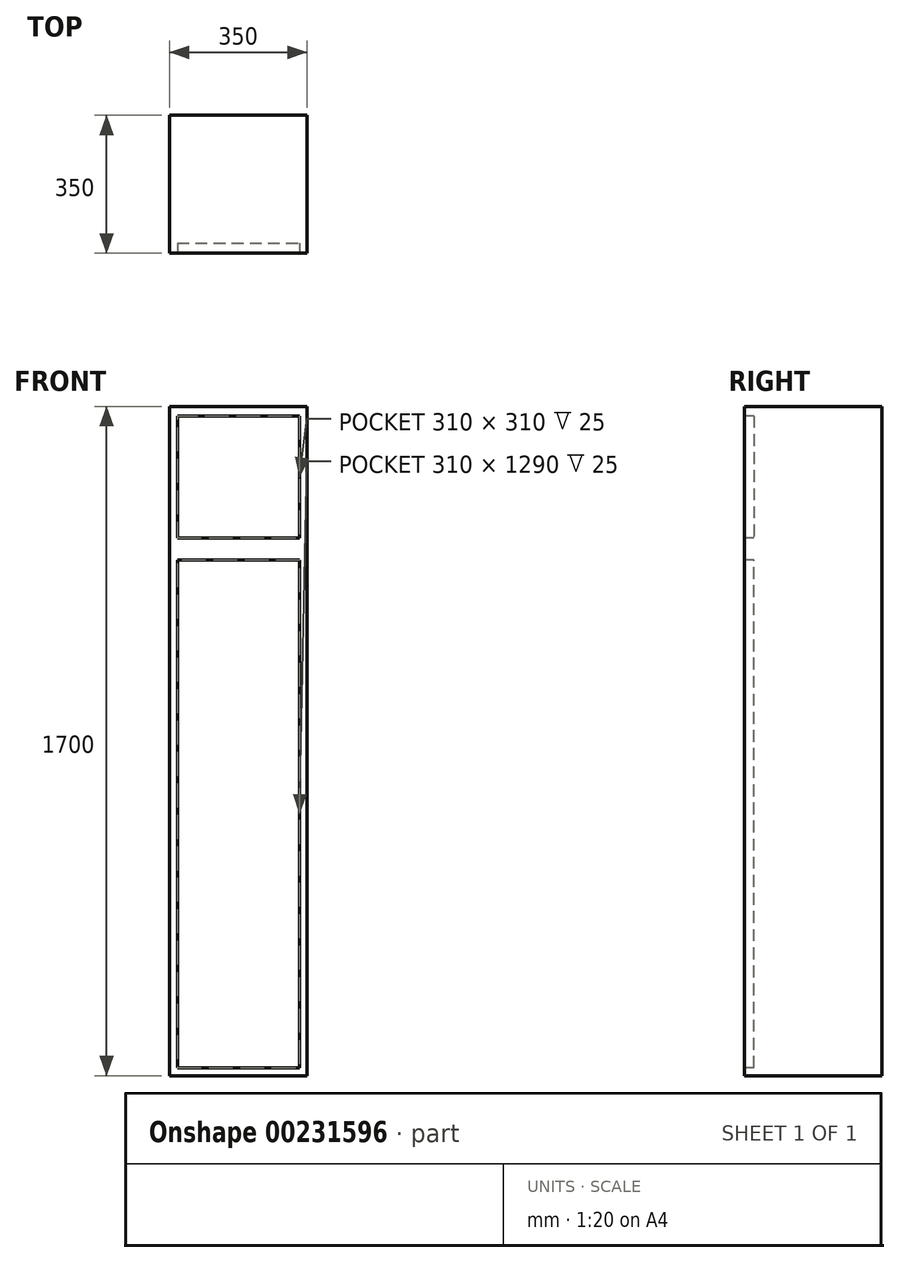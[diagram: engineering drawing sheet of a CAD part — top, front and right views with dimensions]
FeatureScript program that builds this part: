
annotation { "Feature Type Name" : "Feature", "Feature Type Description" : "" }
export const myFeature = defineFeature(function(context is Context, id is Id, definition is map)
    precondition{}
    {
        {
            var Q0;
            Q0=qCreatedBy(makeId("Front.planeOp"),FACE);
            var sketch = newSketch(context, id + "F0", { "sketchPlane" : qUnion([Q0])});
            skLineSegment(sketch, "E0.bottom", {"start": v(-41.38, 1645.43) * mm, "end": v(308.62, 1645.43) * mm});
            skLineSegment(sketch, "E0.top", {"start": v(-41.38, -54.57) * mm, "end": v(308.62, -54.57) * mm});
            skLineSegment(sketch, "E0.left", {"start": v(-41.38, 1645.43) * mm, "end": v(-41.38, -54.57) * mm});
            skLineSegment(sketch, "E0.right", {"start": v(308.62, 1645.43) * mm, "end": v(308.62, -54.57) * mm});
            skSolve(sketch);
        }
        {
            var Q0;
            Q0=makeQuery(id+"F0.imprint","IMPRINT",FACE,{"disambiguationData":[TD([[makeQuery(id+"F0.imprint","IMPRINT",EDGE,{"derivedFrom":sQuery(id+"F0.wireOp",EDGE,"E0.bottom")}),-1.0]])]});
            extrude(context, id + "F1", {"entities" : qUnion([Q0]), "depth" : 350 * mm});
        }
        {
            var Q0;
            Q0=makeQuery(id+"F1.opExtrude","CAP_FACE",FACE,{"disambiguationData":[OSD([sQuery(id+"F0.wireOp",EDGE,"E0.bottom"),sQuery(id+"F0.wireOp",EDGE,"E0.top"),sQuery(id+"F0.wireOp",EDGE,"E0.left"),sQuery(id+"F0.wireOp",EDGE,"E0.right")])],"isStart":false});
            var sketch = newSketch(context, id + "F2", { "sketchPlane" : qUnion([Q0])});
            skLineSegment(sketch, "E1.bottom", {"start": v(-41.38, 1645.43) * mm, "end": v(-21.38, 1645.43) * mm});
            skLineSegment(sketch, "E1.top", {"start": v(-41.38, 1621.67) * mm, "end": v(-21.38, 1621.67) * mm});
            skLineSegment(sketch, "E1.left", {"start": v(-41.38, 1645.43) * mm, "end": v(-41.38, 1621.67) * mm});
            skLineSegment(sketch, "E1.right", {"start": v(-21.38, 1645.43) * mm, "end": v(-21.38, 1621.67) * mm});
            skLineSegment(sketch, "E2.bottom", {"start": v(308.62, 1645.43) * mm, "end": v(288.62, 1645.43) * mm});
            skLineSegment(sketch, "E2.top", {"start": v(308.62, 1625.43) * mm, "end": v(288.62, 1625.43) * mm});
            skLineSegment(sketch, "E2.left", {"start": v(308.62, 1645.43) * mm, "end": v(308.62, 1625.43) * mm});
            skLineSegment(sketch, "E2.right", {"start": v(288.62, 1645.43) * mm, "end": v(288.62, 1625.43) * mm});
            skLineSegment(sketch, "E3.bottom", {"start": v(-21.38, 1621.67) * mm, "end": v(288.62, 1621.67) * mm});
            skLineSegment(sketch, "E3.top", {"start": v(-21.38, 1311.67) * mm, "end": v(288.62, 1311.67) * mm});
            skLineSegment(sketch, "E3.left", {"start": v(-21.38, 1621.67) * mm, "end": v(-21.38, 1311.67) * mm});
            skLineSegment(sketch, "E3.right", {"start": v(288.62, 1621.67) * mm, "end": v(288.62, 1311.67) * mm});
            skLineSegment(sketch, "E4.bottom", {"start": v(-41.38, -54.57) * mm, "end": v(-21.38, -54.57) * mm});
            skLineSegment(sketch, "E4.top", {"start": v(-41.38, -34.57) * mm, "end": v(-21.38, -34.57) * mm});
            skLineSegment(sketch, "E4.left", {"start": v(-41.38, -54.57) * mm, "end": v(-41.38, -34.57) * mm});
            skLineSegment(sketch, "E4.right", {"start": v(-21.38, -54.57) * mm, "end": v(-21.38, -34.57) * mm});
            skLineSegment(sketch, "E5.bottom", {"start": v(308.62, -54.57) * mm, "end": v(288.62, -54.57) * mm});
            skLineSegment(sketch, "E5.top", {"start": v(308.62, -34.57) * mm, "end": v(288.62, -34.57) * mm});
            skLineSegment(sketch, "E5.left", {"start": v(308.62, -54.57) * mm, "end": v(308.62, -34.57) * mm});
            skLineSegment(sketch, "E5.right", {"start": v(288.62, -54.57) * mm, "end": v(288.62, -34.57) * mm});
            skLineSegment(sketch, "E6.bottom", {"start": v(-21.38, -34.57) * mm, "end": v(288.62, -34.57) * mm});
            skLineSegment(sketch, "E6.top", {"start": v(-21.38, 1255.43) * mm, "end": v(288.62, 1255.43) * mm});
            skLineSegment(sketch, "E6.left", {"start": v(-21.38, -34.57) * mm, "end": v(-21.38, 1255.43) * mm});
            skLineSegment(sketch, "E6.right", {"start": v(288.62, -34.57) * mm, "end": v(288.62, 1255.43) * mm});
            skSolve(sketch);
        }
        {
            var Q0;
            Q0=makeQuery(id+"F2.imprint","IMPRINT",FACE,{"disambiguationData":[TD([[makeQuery(id+"F2.imprint","IMPRINT",EDGE,{"derivedFrom":sQuery(id+"F2.wireOp",EDGE,"E6.bottom")}),1.0]])]});
            var Q1;
            Q1=makeQuery(id+"F2.imprint","IMPRINT",FACE,{"disambiguationData":[TD([[makeQuery(id+"F2.imprint","IMPRINT",EDGE,{"derivedFrom":sQuery(id+"F2.wireOp",EDGE,"E3.bottom")}),-1.0]])]});
            extrude(context, id + "F3", {"entities" : qUnion([Q0, Q1]), "operationType" : NewBodyOperationType.REMOVE, "oppositeDirection" : true, "depth" : 25 * mm});
        }
    });
